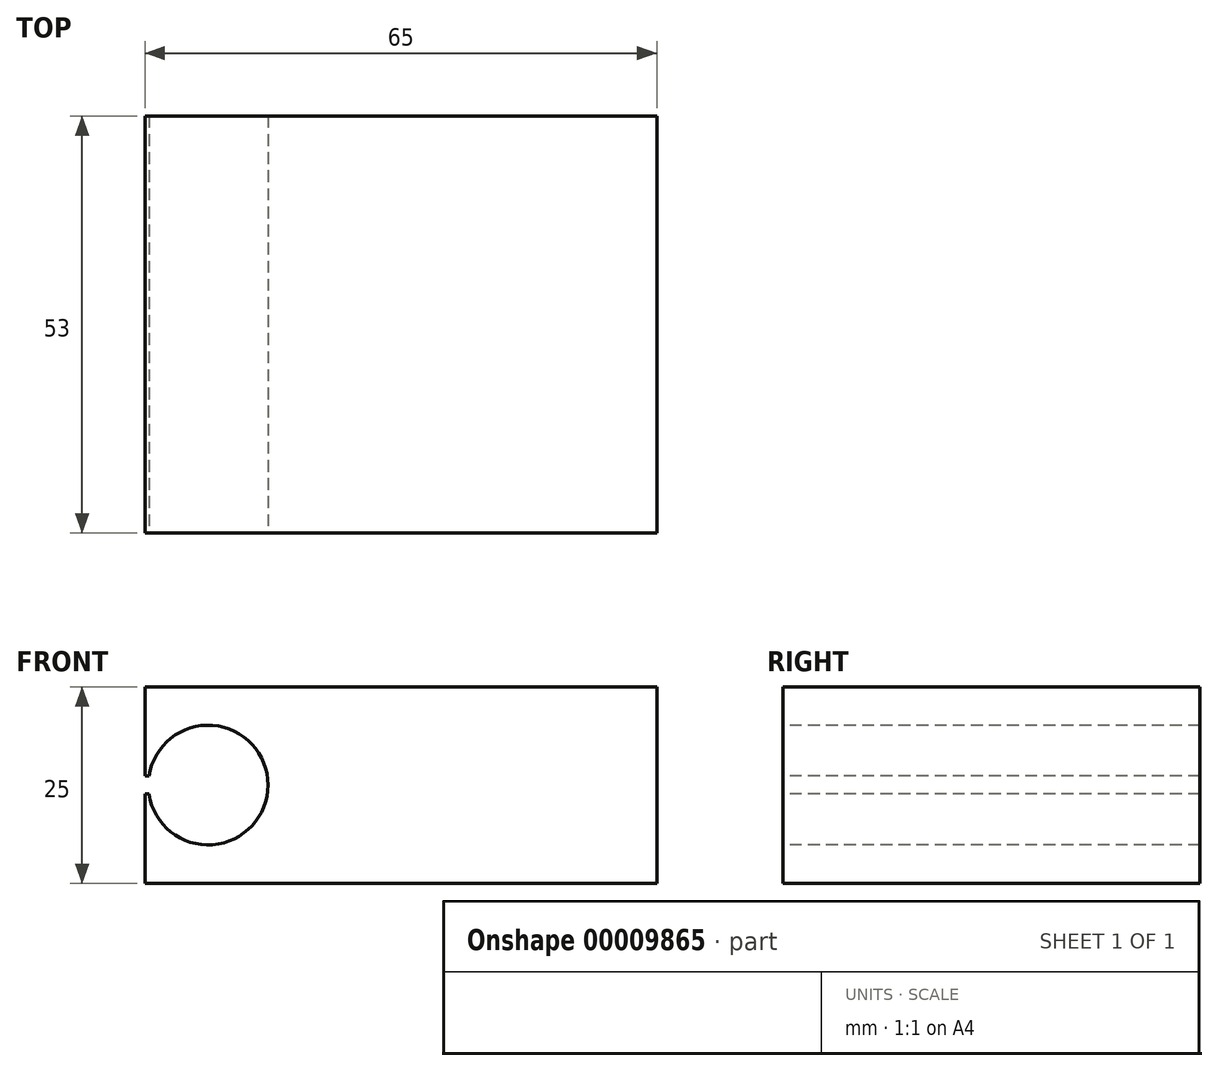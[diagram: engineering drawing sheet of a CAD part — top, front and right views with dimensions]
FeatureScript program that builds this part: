
annotation { "Feature Type Name" : "Feature", "Feature Type Description" : "" }
export const myFeature = defineFeature(function(context is Context, id is Id, definition is map)
    precondition{}
    {
        {
            var Q0;
            Q0=qCreatedBy(makeId("Top.planeOp"),FACE);
            var sketch = newSketch(context, id + "F0", { "sketchPlane" : qUnion([Q0])});
            skLineSegment(sketch, "E0.bottom", {"start": v(0, 0) * mm, "end": v(65, 0) * mm});
            skLineSegment(sketch, "E0.top", {"start": v(0, 53) * mm, "end": v(65, 53) * mm});
            skLineSegment(sketch, "E0.left", {"start": v(0, 0) * mm, "end": v(0, 53) * mm});
            skLineSegment(sketch, "E0.right", {"start": v(65, 0) * mm, "end": v(65, 53) * mm});
            skSolve(sketch);
        }
        {
            var Q0;
            Q0 = qSketchRegion(id + "F0", true);
            extrude(context, id + "F1", {"entities" : qUnion([Q0]), "depth" : 25 * mm});
        }
        {
            var Q0;
            Q0=makeQuery(id+"F1.opExtrude","SWEPT_FACE",FACE,{"disambiguationData":[OSD([sQuery(id+"F0.wireOp",EDGE,"E0.bottom")])]});
            var sketch = newSketch(context, id + "F2", { "sketchPlane" : qUnion([Q0])});
            skCircle(sketch, "E1", {"center": v(8, 12.5) * mm, "radius": 7.6 * mm});
            skPoint(sketch, "E1.centerSnap0", {"position": v(0, 12.5) * mm});
            skLineSegment(sketch, "E2.bottom", {"start": v(0, 13.64) * mm, "end": v(0.49, 13.64) * mm});
            skLineSegment(sketch, "E2.top", {"start": v(0, 11.36) * mm, "end": v(0.49, 11.36) * mm});
            skLineSegment(sketch, "E2.left", {"start": v(0, 11.36) * mm, "end": v(0, 13.64) * mm});
            skLineSegment(sketch, "E2.right", {"start": v(0.49, 11.36) * mm, "end": v(0.49, 13.64) * mm});
            skPoint(sketch, "E3", {"position": v(0.49, 12.5) * mm});
            skSolve(sketch);
        }
        {
            var Q0;
            Q0 = qSketchRegion(id + "F2", true);
            extrude(context, id + "F3", {"entities" : qUnion([Q0]), "operationType" : NewBodyOperationType.REMOVE, "endBound" : BoundingType.THROUGH_ALL, "oppositeDirection" : true, "depth" : 25 * mm});
        }
    });
